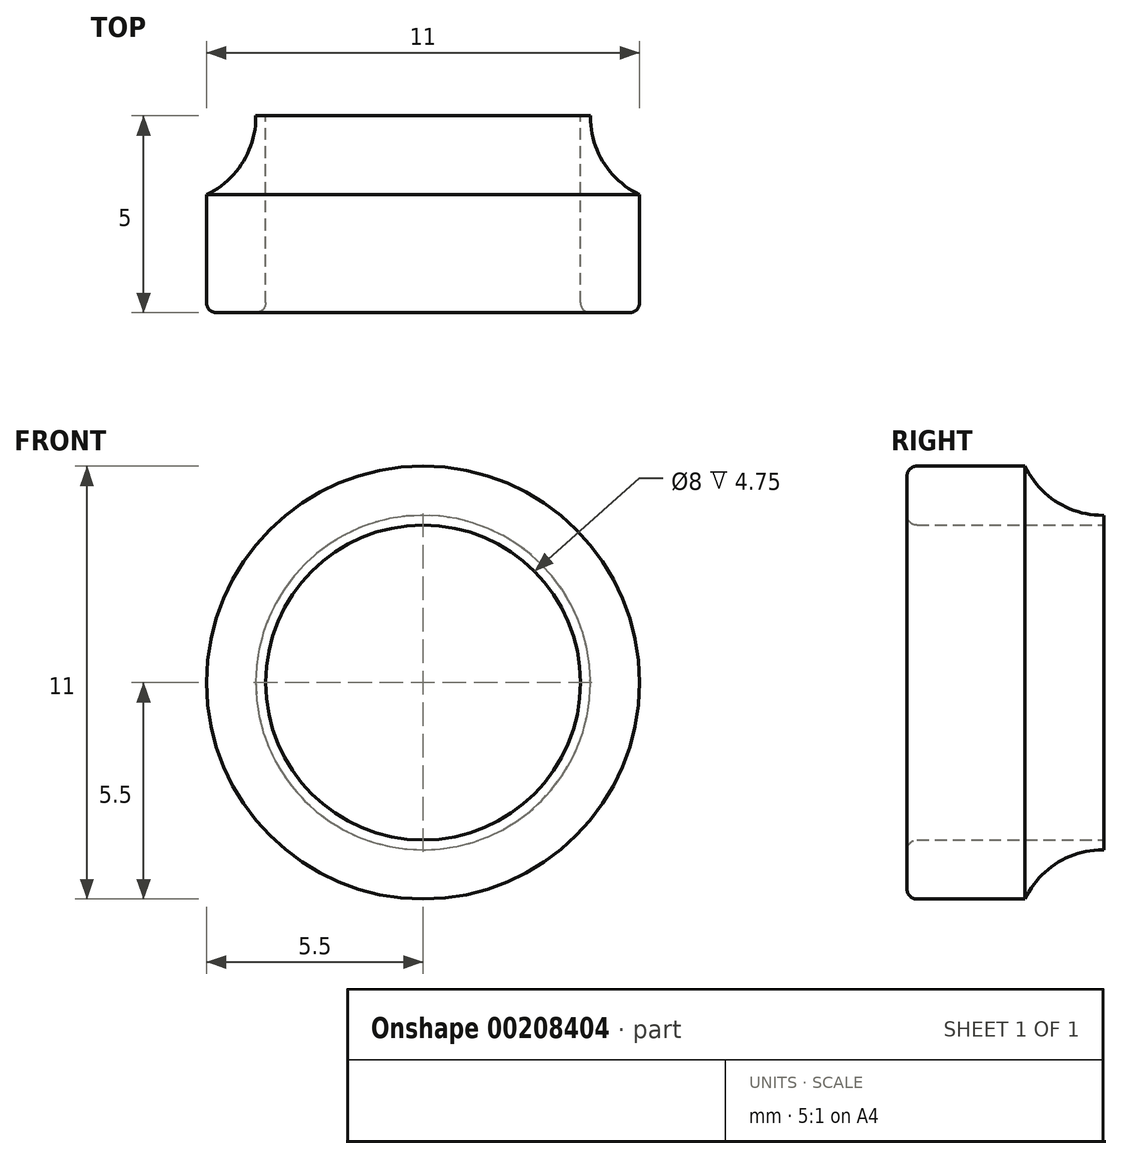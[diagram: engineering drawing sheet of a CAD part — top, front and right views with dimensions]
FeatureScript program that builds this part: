
annotation { "Feature Type Name" : "Feature", "Feature Type Description" : "" }
export const myFeature = defineFeature(function(context is Context, id is Id, definition is map)
    precondition{}
    {
        {
            var Q0;
            Q0=qCreatedBy(makeId("Front.planeOp"),FACE);
            var sketch = newSketch(context, id + "F0", { "sketchPlane" : qUnion([Q0])});
            skCircle(sketch, "E0", {"center": v(0, 0) * mm, "radius": 5.5 * mm});
            skCircle(sketch, "E1", {"center": v(0, 0) * mm, "radius": 4 * mm});
            skSolve(sketch);
        }
        {
            var Q0;
            Q0=makeQuery(id+"F0.imprint","IMPRINT",FACE,{"disambiguationData":[TD([[makeQuery(id+"F0.imprint","IMPRINT",EDGE,{"derivedFrom":sQuery(id+"F0.wireOp",EDGE,"E0")}),1.0]])]});
            var Q1;
            Q1=sQuery(id+"F0.wireOp",EDGE,"E1");
            extrude(context, id + "F4", {"entities" : qUnion([Q0]), "surfaceEntities" : qUnion([Q1]), "depth" : 5 * mm});
        }
        {
            var Q0;
            Q0=makeQuery(id+"F4.opExtrude","CAP_EDGE",EDGE,{"disambiguationData":[OSD([sQuery(id+"F0.wireOp",EDGE,"E1")])],"isStart":false});
            fillet(context, id + "F5", {"entities" : qUnion([Q0]), "radius" : 0.25 * mm, "tangentPropagation" : true, "allowEdgeOverflow" : false});
        }
        {
            var Q0;
            Q0=makeQuery(id+"F4.opExtrude","CAP_EDGE",EDGE,{"disambiguationData":[OSD([sQuery(id+"F0.wireOp",EDGE,"E0")])],"isStart":false});
            fillet(context, id + "F6", {"entities" : qUnion([Q0]), "radius" : 0.25 * mm, "tangentPropagation" : true, "allowEdgeOverflow" : false});
        }
        {
            var Q0;
            Q0=makeQuery(id+"F4.opExtrude","CAP_FACE",FACE,{"disambiguationData":[OSD([sQuery(id+"F0.wireOp",EDGE,"E0"),sQuery(id+"F0.wireOp",EDGE,"E1")])],"isStart":true});
            var sketch = newSketch(context, id + "F1", { "sketchPlane" : qUnion([Q0])});
            skCircle(sketch, "E2", {"center": v(0, 0) * mm, "radius": 4.25 * mm});
            skSolve(sketch);
        }
        {
            var Q0;
            Q0=makeQuery(id+"F1.imprint","IMPRINT",FACE,{"disambiguationData":[TD([[makeQuery(id+"F1.imprint","IMPRINT",EDGE,{"derivedFrom":sQuery(id+"F1.wireOp",EDGE,"E2")}),-1.0]])]});
            var Q1;
            Q1=sQuery(id+"F1.wireOp",EDGE,"E2");
            extrude(context, id + "F2", {"entities" : qUnion([Q0]), "operationType" : NewBodyOperationType.REMOVE, "surfaceEntities" : qUnion([Q1]), "oppositeDirection" : true, "depth" : 2 * mm});
        }
        {
            var Q0;
            Q0=makeQuery(id+"F2.boolean.opBoolean","COPY",EDGE,{"derivedFrom":makeQuery(id+"F2.opExtrude","CAP_EDGE",EDGE,{"disambiguationData":[OSD([sQuery(id+"F1.wireOp",EDGE,"E2")])],"isStart":false})});
            fillet(context, id + "F3", {"entities" : qUnion([Q0]), "radius" : 2.18 * mm, "tangentPropagation" : true, "allowEdgeOverflow" : false});
        }
    });
